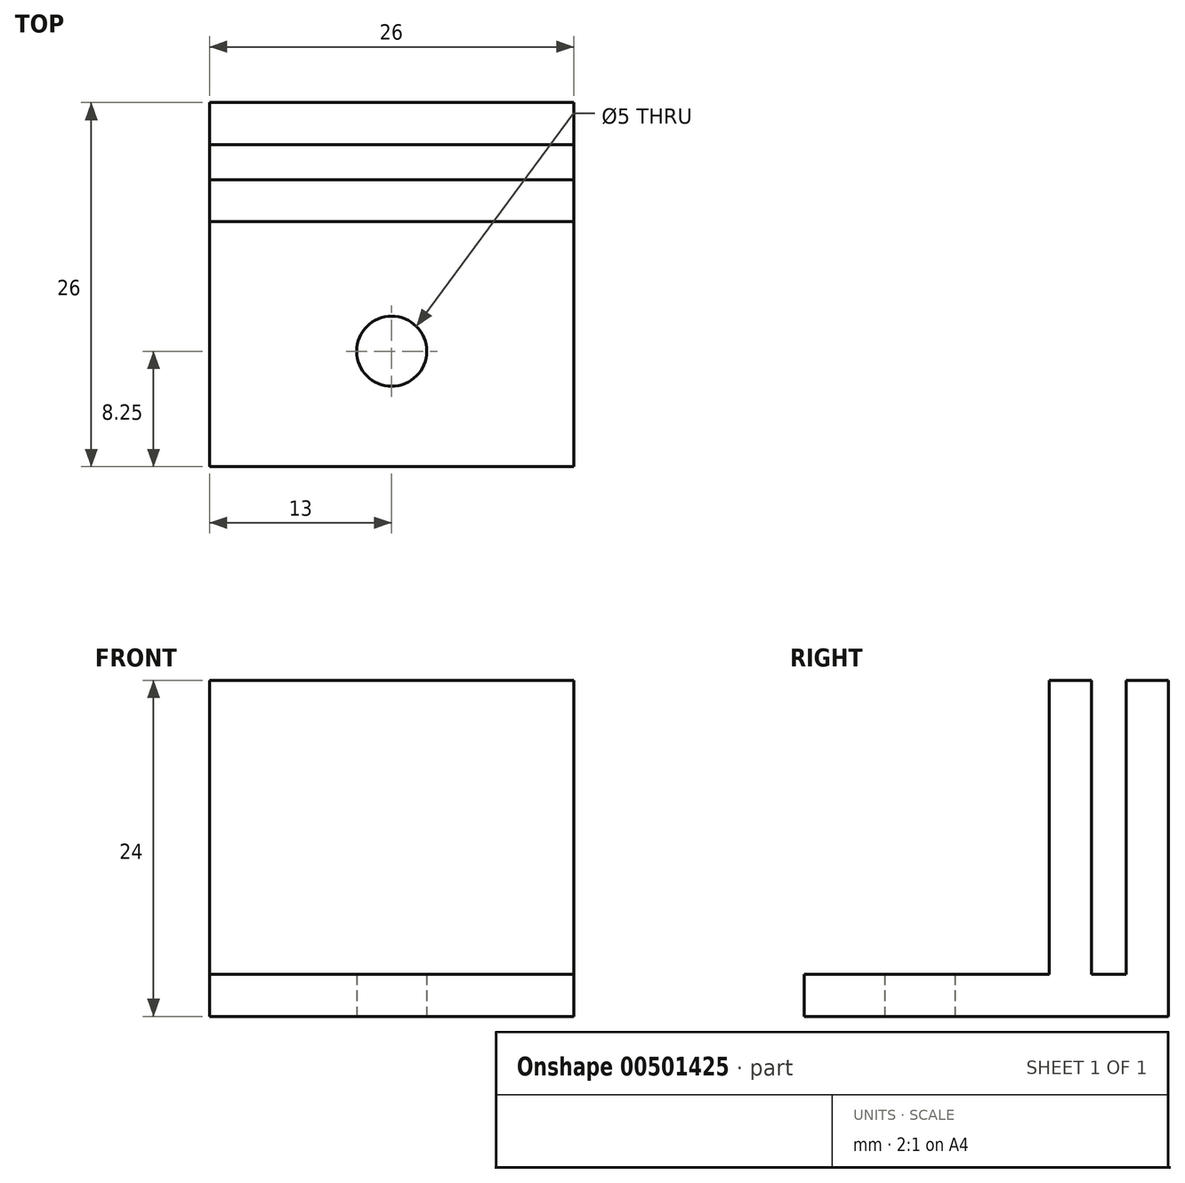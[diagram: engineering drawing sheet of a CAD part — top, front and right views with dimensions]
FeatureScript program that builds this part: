
annotation { "Feature Type Name" : "Feature", "Feature Type Description" : "" }
export const myFeature = defineFeature(function(context is Context, id is Id, definition is map)
    precondition{}
    {
        {
            var Q0;
            Q0=qCreatedBy(makeId("Top.planeOp"),FACE);
            var sketch = newSketch(context, id + "F0", { "sketchPlane" : qUnion([Q0])});
            skLineSegment(sketch, "E0.bottom", {"start": v(13, -13) * mm, "end": v(-13, -13) * mm});
            skLineSegment(sketch, "E0.top", {"start": v(13, 13) * mm, "end": v(-13, 13) * mm});
            skLineSegment(sketch, "E0.left", {"start": v(13, -13) * mm, "end": v(13, 13) * mm});
            skLineSegment(sketch, "E0.right", {"start": v(-13, -13) * mm, "end": v(-13, 13) * mm});
            skPoint(sketch, "E0.middle", {"position": v(0, 0) * mm});
            skLineSegment(sketch, "E1", {"start": v(-13, 10) * mm, "end": v(13, 10) * mm});
            skLineSegment(sketch, "E2", {"start": v(13, 7.5) * mm, "end": v(-13, 7.5) * mm});
            skLineSegment(sketch, "E3", {"start": v(-13, 4.5) * mm, "end": v(13, 4.5) * mm});
            skPoint(sketch, "E4", {"position": v(13, 4.5) * mm});
            skPoint(sketch, "E5", {"position": v(13, 7.5) * mm});
            skPoint(sketch, "E6", {"position": v(13, 10) * mm});
            skPoint(sketch, "E7", {"position": v(13, 13) * mm});
            skPoint(sketch, "E8", {"position": v(-13, 13) * mm});
            skPoint(sketch, "E9", {"position": v(-13, 10) * mm});
            skPoint(sketch, "E10", {"position": v(-13, 7.5) * mm});
            skPoint(sketch, "E11", {"position": v(-13, 4.5) * mm});
            skPoint(sketch, "E12", {"position": v(-13, -13) * mm});
            skPoint(sketch, "E13", {"position": v(13, -13) * mm});
            skLineSegment(sketch, "E14", {"start": v(0, -13) * mm, "end": v(0, -4.75) * mm});
            skPoint(sketch, "E14.endSnap0", {"position": v(0, -13) * mm});
            skCircle(sketch, "E15", {"center": v(0, -4.75) * mm, "radius": 2.5 * mm});
            skSolve(sketch);
        }
        {
            var Q0;
            {var subQ0=sQuery(id+"F0.wireOp",EDGE,"E0.top");Q0=makeQuery(id+"F0.imprint","IMPRINT",FACE,{"disambiguationData":[TD([[makeQuery(id+"F0.imprint","IMPRINT",EDGE,{"derivedFrom":subQ0}),1.0]])]});}
            var Q1;
            {var subQ0=sQuery(id+"F0.wireOp",EDGE,"E2");Q1=makeQuery(id+"F0.imprint","IMPRINT",FACE,{"disambiguationData":[TD([[makeQuery(id+"F0.imprint","IMPRINT",EDGE,{"derivedFrom":subQ0}),1.0]])]});}
            extrude(context, id + "F1", {"entities" : qUnion([Q0, Q1]), "depth" : 24 * mm});
        }
        {
            var Q0;
            {var subQ0=sQuery(id+"F0.wireOp",EDGE,"E0.top");Q0=makeQuery(id+"F0.imprint","IMPRINT",FACE,{"disambiguationData":[TD([[makeQuery(id+"F0.imprint","IMPRINT",EDGE,{"derivedFrom":subQ0}),1.0]])]});}
            var Q1;
            {var subQ0=sQuery(id+"F0.wireOp",EDGE,"E1");Q1=makeQuery(id+"F0.imprint","IMPRINT",FACE,{"disambiguationData":[TD([[makeQuery(id+"F0.imprint","IMPRINT",EDGE,{"derivedFrom":subQ0}),-1.0]])]});}
            var Q2;
            {var subQ0=sQuery(id+"F0.wireOp",EDGE,"E2");Q2=makeQuery(id+"F0.imprint","IMPRINT",FACE,{"disambiguationData":[TD([[makeQuery(id+"F0.imprint","IMPRINT",EDGE,{"derivedFrom":subQ0}),1.0]])]});}
            var Q3;
            {var subQ3=sQuery(id+"F0.wireOp",EDGE,"E3");Q3=makeQuery(id+"F0.imprint","IMPRINT",FACE,{"disambiguationData":[TD([[makeQuery(id+"F0.imprint","IMPRINT",EDGE,{"derivedFrom":subQ3}),-1.0]])]});}
            extrude(context, id + "F2", {"entities" : qUnion([Q0, Q1, Q2, Q3]), "operationType" : NewBodyOperationType.ADD, "depth" : 3 * mm});
        }
    });
